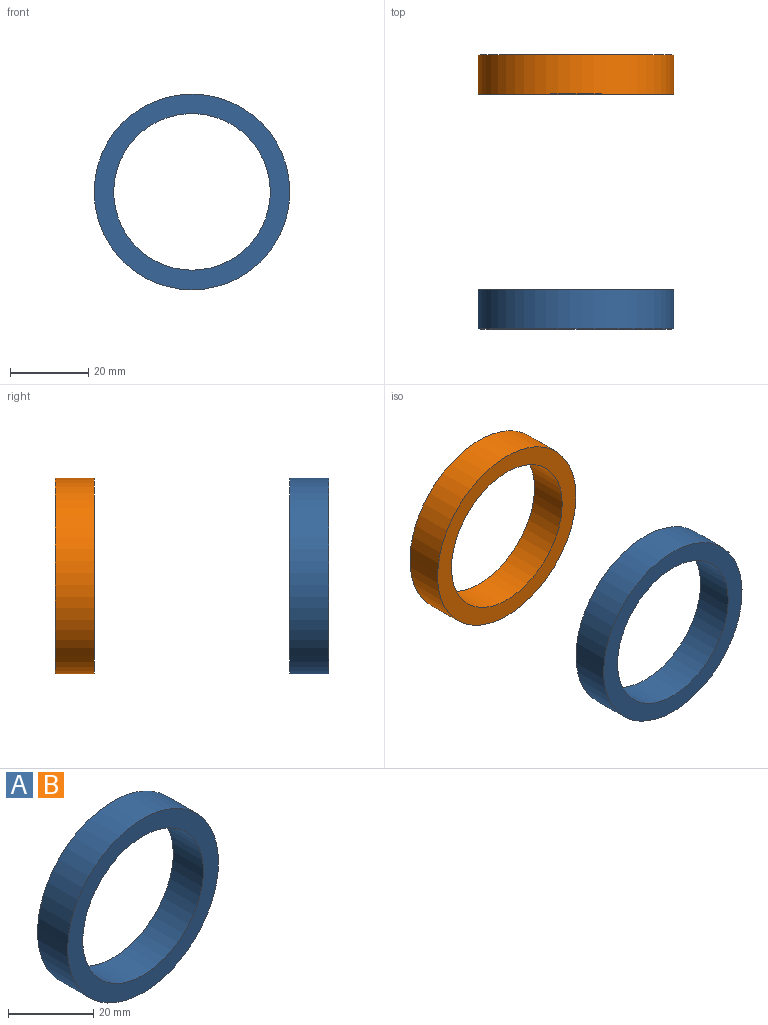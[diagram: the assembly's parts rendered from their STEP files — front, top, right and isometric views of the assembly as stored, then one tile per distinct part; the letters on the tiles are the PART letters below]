
ASSEMBLY  parts=2 mates=1
PART A: 4 faces, bbox 50x10x50 mm
  f0: cylinder r=20mm len=40mm, axis (0,1,0), area 1256.6mm2, adj f2,f3
  f1: cylinder r=25mm len=50mm, axis (0,1,0), area 1570.8mm2, adj f2,f3
  f2: plane 50x50mm, normal (0,-1,0), area 706.9mm2, adj f0,f1
  f3: plane 50x50mm, normal (0,1,0), area 706.9mm2, adj f0,f1
PART B: same geometry as A
PLACE A t=(0,-60,0)mm
PLACE B at identity fixed
MATE slider B.f0 <-> A.f0  axis (0,1,0) through (0,-10,0)mm
